# Revit family: Haworth_EncloseFrameless_Accessories_WallModuleIntersection
name_source: partatom
category: Furniture Systems
revit_build: Autodesk Revit 2018 (Build: 20170223_1515(x64)
units: mm (PartAtom-declared; Revit-internal decimal feet)

## family parameters
Always vertical = Yes
Cut with Voids When Loaded = No
OmniClass Number = 23.25.40.14
OmniClass Title = Demountable Partitions
Part Type = Normal
Room Calculation Point = No
Round Connector Dimension = Use Diameter
Shared = No
Work Plane-Based = No

## types (6) — shared parameters
Actual Height = 108 "
Angle A = 80.00°
Angle B = 10.00°
Assembly Code = C1010200
Depth = 4 "
Description = Accessories-Wall_Module-Intersection
Frame Finish = Haworth _ Metal _ Brushed Aluminum
Height = 108 "
Manufacturer = Haworth
Material Options = http://surfaces.haworth.com
Max. Height = 144 "
Min. Height = 84 "
Min/Max Height = 84-144 in.
Model = Haworth - Enclose Frameless
Revision Number = 3
Sustainability Info = http://www.haworth.com
URL = www.haworth.com
URL - Product = http://www.haworth.com
Variable Angle = 20.00°
Variable Angle Note = Angle for Variable Angle Post Only
Warranty = http://www.haworth.com

## per-type parameters (varying)
| type | 2 Way 135 | 2 Way 180 Rectangular | 2 Way 180 Square | 2 Way Square Corner | 3 Way Square | Wdith |
| 2 Way_135 | Yes | No | No | No | No | 4 " |
| 3 Way_90 | No | No | No | No | Yes | 4 " |
| 2 Way_90 | No | No | No | Yes | No | 4 " |
| 2 Way_180 | No | No | Yes | No | No | 4 " |
| 2 Way Variable Angle | No | No | No | No | No | 4 " |
| 2 Way_180_6in. | No | Yes | No | No | No | 6 " |

type visibility flags (boolean, named after types; folded from table):
- 2 Way_135: Yes: (none)
- 3 Way_90: Yes: (none)
- 2 Way_90: Yes: (none)
- 2 Way_180: Yes: (none)
- 2 Way Variable Angle: Yes: 2 Way Variable Angle
- 2 Way_180_6in.: Yes: (none)

## geometry (parser evidence)
native form markers: Sweep x4
no freeform markers — native parametric forms only
